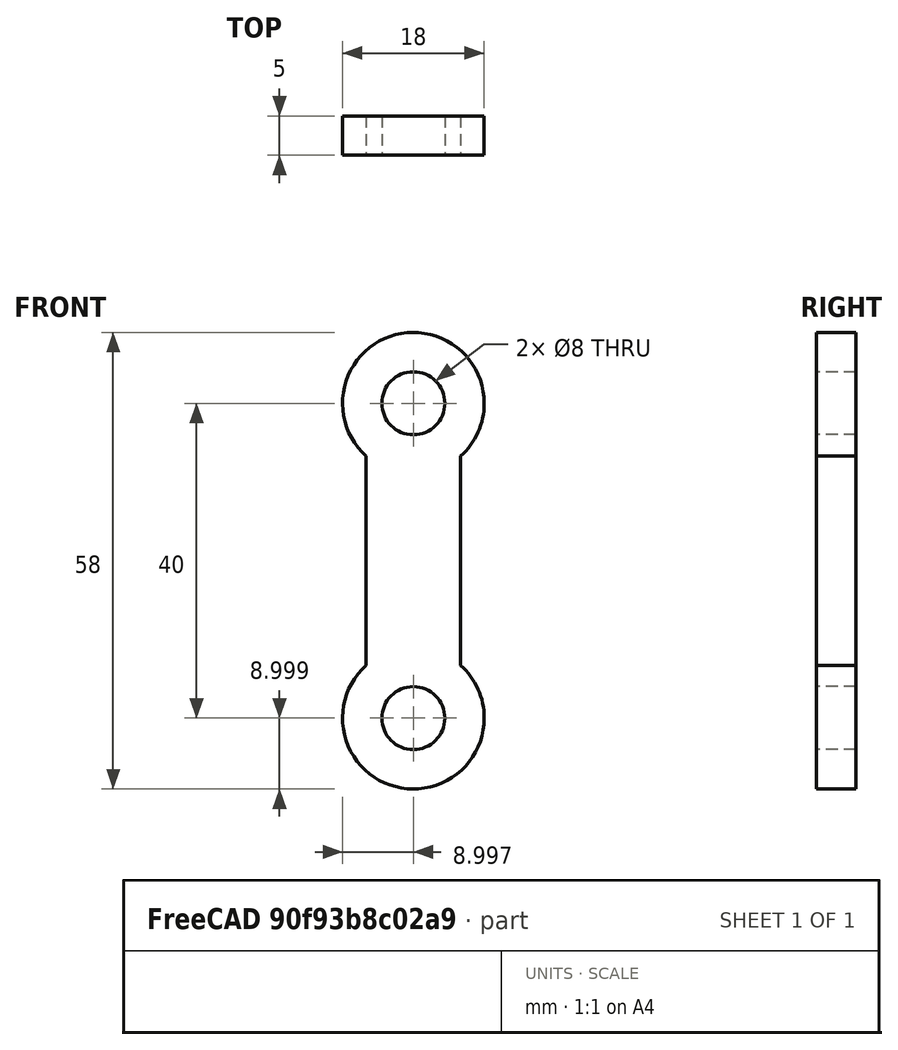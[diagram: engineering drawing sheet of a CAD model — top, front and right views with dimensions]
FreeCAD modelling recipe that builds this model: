
FCSTD DOCUMENT  (FreeCAD 0.18R16110 (Git))
Label: connecting-rod
License: All rights reserved
LicenseURL: http://en.wikipedia.org/wiki/All_rights_reserved
objects: Part::Cylinder×2, Part::Cut×2, Part::Box×1, Part::MultiFuse×1, Mesh::Feature×1
note: 6 computed .brp shape members not serialized (recipe doc carries the construction recipe); baked Part::Feature solids carry a one-line shape summary decoded from their .brp

FEATURE [Part::Cylinder] Cylinder013  label="Zylinder013"
  Angle = 360
  AttacherType = Attacher::AttachEngine3D
  Height = 10
  Placement = pos=(0,30,-5) rot=(0,0,1;0rad)
  Radius = 4
FEATURE [Part::Cylinder] Cylinder012  label="Zylinder012"
  Angle = 360
  AttacherType = Attacher::AttachEngine3D
  Height = 5
  Placement = pos=(0,30,-5) rot=(0,0,1;0rad)
  Radius = 9
FEATURE [Part::Cut] Cut007
  Base = -> Cylinder012
  Tool = -> Cylinder013
FEATURE [Part::Cut] Cut008
  Base = -> Cylinder012
  Placement = pos=(0,-40,0) rot=(0,0,1;0rad)
  Tool = -> Cylinder013
FEATURE [Part::Box] Box004  label="Quader004"
  AttacherType = Attacher::AttachEngine3D
  Height = 5
  Length = 12
  Placement = pos=(-6,-4,-5) rot=(0,0,1;0rad)
  Width = 28
FEATURE [Part::MultiFuse] Fusion012  label="connecting-rod"
  Placement = pos=(-4.90272,18,22.4793) rot=(1,0,0;1.5708rad)
  Shapes = -> [Cut007,Cut008,Box004]
FEATURE [Mesh::Feature] Mesh  label="connecting-rod (Meshed)"
